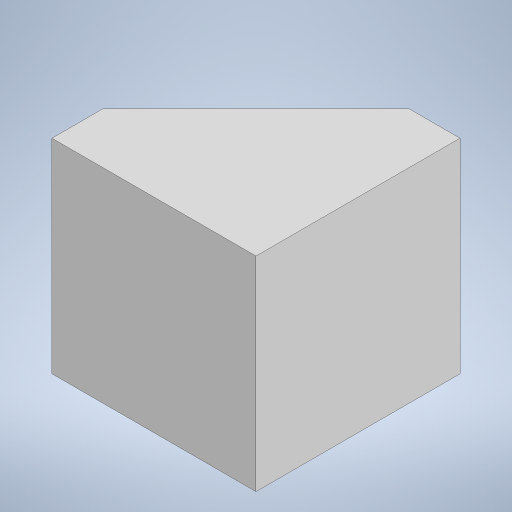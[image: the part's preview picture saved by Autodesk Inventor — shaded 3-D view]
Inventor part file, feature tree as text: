
AUTODESK INVENTOR PART (.ipt)
format: ipt  version: 2023 (Build 270158000, 158)  size: 210,944 bytes
history: native  units: mm
features: extrude x4, sketch x4
ambient origin geometry x8: Origin, YZ Plane, XZ Plane, XY Plane, X Axis, Y Axis, Z Axis, Center Point
bodies: Body1 (feature_tree)
feature tree (8):
  extrude  "Extrusion22"  Depth=20.0mm
  extrude  "Extrusion23"  Depth=20.0mm
  extrude  "Extrusion24"  Depth=5.0mm TaperAngle=0.0deg
  extrude  "Extrusion25"  Depth=5.0mm
  sketch  "Sketch30"  dims[d101=20.0mm d102=20.0mm]
  sketch  "Sketch31"  dims[d103=5.0mm d104=0.0mm d105=20.0mm]
  sketch  "Sketch32"  dims[d106=5.0mm d107=0.0mm d108=5.0mm d109=0.0mm]
  sketch  "Sketch33"  dims[d110=5.0mm d111=0.0mm d49=0.5mm d50=0.872665mm d51=0.5mm d52=0.872665mm]
